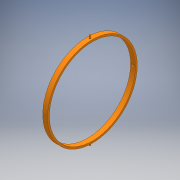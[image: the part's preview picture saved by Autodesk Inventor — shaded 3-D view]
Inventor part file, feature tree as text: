
AUTODESK INVENTOR PART (.ipt)
format: ipt  version: 2018 (Build 220112000, 112)  size: 160,768 bytes
history: native  units: mm
features: extrude x6, sketch x6, plane x4, other x1, mirror x1, projected_geometry x1
ambient origin geometry x8: Origin, YZ Plane, XZ Plane, XY Plane, X Axis, Y Axis, Z Axis, Center Point
bodies: Solid1 (feature_tree)
feature tree (19):
  extrude  "Extrusion1"  Depth=188.0mm
  plane  "Work Plane1"
  extrude  "Extrusion2"  Depth=10.0mm
  plane  "Work Plane2"
  extrude  "Extrusion3"  Depth=230.0mm TaperAngle=0.0deg
  plane  "Work Plane3"
  extrude  "Extrusion4"  Depth=5.0mm TaperAngle=0.0deg
  other  "Work Axis1"
  plane  "Work Plane4"
  extrude  "Extrusion5"  Depth=6.0mm
  mirror  "Mirror1"
  extrude  "Extrusion6"  Depth=3.0mm
  sketch  "Sketch1"  dims[d0=180.0mm d1=188.0mm]
  sketch  "Sketch2"  dims[d2=10.0mm d3=0.0mm d4=6.0mm]
  projected_geometry  "Projected Loop1"
  sketch  "Sketch3"  dims[d5=3.0mm d6=230.0mm d7=0.0mm]
  sketch  "Sketch4"  dims[d8=6.0mm d9=5.0mm d10=0.0mm]
  sketch  "Sketch5"  dims[d11=-4.0mm d12=6.0mm]
  sketch  "Sketch6"  dims[d13=5.0mm d14=0.0mm d15=3.0mm d16=12.0mm d17=0.0mm d18=8.0mm d19=0.0mm]
